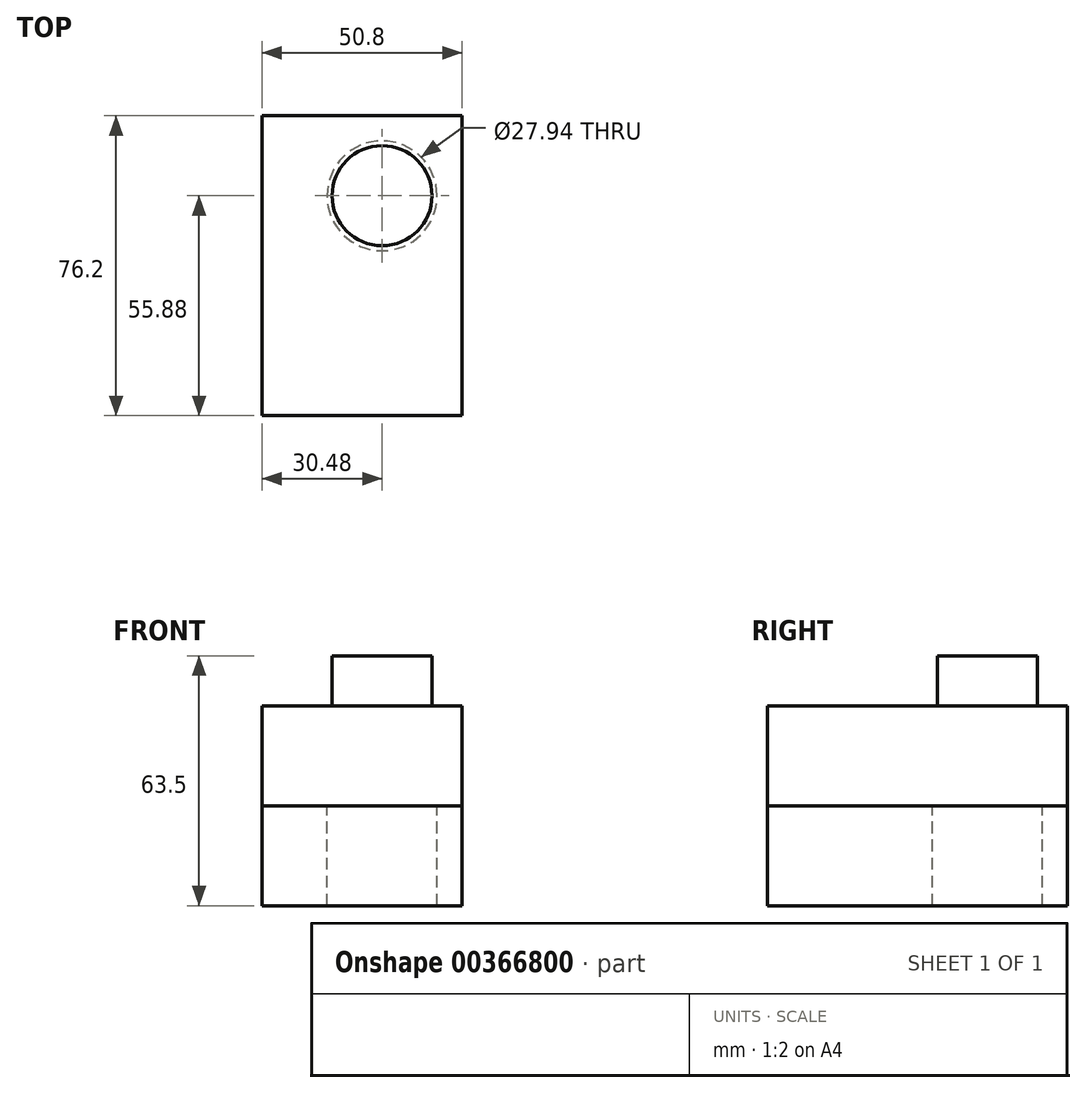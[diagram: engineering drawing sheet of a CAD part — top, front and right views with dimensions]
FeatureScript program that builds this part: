
annotation { "Feature Type Name" : "Feature", "Feature Type Description" : "" }
export const myFeature = defineFeature(function(context is Context, id is Id, definition is map)
    precondition{}
    {
        {
            var Q0;
            Q0=qCreatedBy(makeId("Top.planeOp"),FACE);
            var sketch = newSketch(context, id + "F0", { "sketchPlane" : qUnion([Q0])});
            skLineSegment(sketch, "E0.bottom", {"start": v(25.4, 38.1) * mm, "end": v(-25.4, 38.1) * mm});
            skLineSegment(sketch, "E0.top", {"start": v(25.4, -38.1) * mm, "end": v(-25.4, -38.1) * mm});
            skLineSegment(sketch, "E0.left", {"start": v(25.4, 38.1) * mm, "end": v(25.4, -38.1) * mm});
            skLineSegment(sketch, "E0.right", {"start": v(-25.4, 38.1) * mm, "end": v(-25.4, -38.1) * mm});
            skPoint(sketch, "E0.middle", {"position": v(0, 0) * mm});
            skSolve(sketch);
        }
        {
            var Q0;
            Q0=makeQuery(id+"F0.imprint","IMPRINT",FACE,{"disambiguationData":[TD([[makeQuery(id+"F0.imprint","IMPRINT",EDGE,{"derivedFrom":sQuery(id+"F0.wireOp",EDGE,"E0.bottom")}),1.0]])]});
            extrude(context, id + "F1", {"entities" : qUnion([Q0]), "depth" : 25.4 * mm});
        }
        {
            var Q0;
            Q0=makeQuery(id+"F1.opExtrude","CAP_FACE",FACE,{"disambiguationData":[OSD([sQuery(id+"F0.wireOp",EDGE,"E0.bottom"),sQuery(id+"F0.wireOp",EDGE,"E0.top"),sQuery(id+"F0.wireOp",EDGE,"E0.left"),sQuery(id+"F0.wireOp",EDGE,"E0.right")])],"isStart":false});
            var sketch = newSketch(context, id + "F2", { "sketchPlane" : qUnion([Q0])});
            skCircle(sketch, "E1", {"center": v(5.08, 17.78) * mm, "radius": 12.7 * mm});
            skSolve(sketch);
        }
        {
            var Q0;
            Q0=makeQuery(id+"F2.imprint","IMPRINT",FACE,{"disambiguationData":[TD([[makeQuery(id+"F2.imprint","IMPRINT",EDGE,{"derivedFrom":sQuery(id+"F2.wireOp",EDGE,"E1")}),1.0]])]});
            extrude(context, id + "F3", {"entities" : qUnion([Q0]), "operationType" : NewBodyOperationType.ADD, "depth" : 12.7 * mm});
        }
        {
            var Q0;
            Q0=qCreatedBy(makeId("Top.planeOp"),FACE);
            var sketch = newSketch(context, id + "F4", { "sketchPlane" : qUnion([Q0])});
            skLineSegment(sketch, "E2.0", {"start": v(25.4, 38.1) * mm, "end": v(-25.4, 38.1) * mm});
            skLineSegment(sketch, "E3.0", {"start": v(25.4, 38.1) * mm, "end": v(25.4, -38.1) * mm});
            skLineSegment(sketch, "E4.0", {"start": v(25.4, -38.1) * mm, "end": v(-25.4, -38.1) * mm});
            skLineSegment(sketch, "E5.0", {"start": v(-25.4, 38.1) * mm, "end": v(-25.4, -38.1) * mm});
            skCircle(sketch, "E6.0", {"center": v(5.08, 17.78) * mm, "radius": 12.7 * mm});
            skCircle(sketch, "E7.0", {"center": v(5.08, 17.78) * mm, "radius": 13.97 * mm});
            skSolve(sketch);
        }
        {
            var Q0;
            Q0=makeQuery(id+"F4.imprint","IMPRINT",FACE,{"disambiguationData":[TD([[makeQuery(id+"F4.imprint","IMPRINT",EDGE,{"derivedFrom":sQuery(id+"F4.wireOp",EDGE,"E2.0")}),1.0]])]});
            extrude(context, id + "F5", {"entities" : qUnion([Q0]), "oppositeDirection" : true, "depth" : 25.4 * mm});
        }
    });
